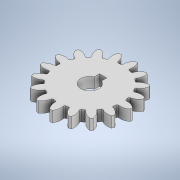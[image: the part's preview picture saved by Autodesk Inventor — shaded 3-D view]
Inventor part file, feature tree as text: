
AUTODESK INVENTOR PART (.ipt)
format: ipt  version: 2020 (Build 240168000, 168)  size: 262,656 bytes
history: native  units: mm
features: extrude x2, sketch x2, pattern_circular x1
ambient origin geometry x8: Origin, YZ Plane, XZ Plane, XY Plane, X Axis, Y Axis, Z Axis, Center Point
bodies: Solid1 (feature_tree)
feature tree (5):
  extrude  "Extrusion1"  Depth=3.0mm
  pattern_circular  "Circular Pattern2"  [2 undecoded]
  extrude  "Extrusion2"  TaperAngle=0.0deg  [1 undecoded]
  sketch  "Sketch1"  dims[d4=3.0mm d5=0.0mm d13=5.0mm]
  sketch  "Sketch2"  dims[d14=2.0mm d15=3.7mm d16=0.0mm d17=0.0mm d18=170.0mm d19=360.0deg d23=21.0mm d25=1.544118mm d26=1.235294mm d27=3.490659mm d28=19.733545mm d29=3.490659mm d30=0.308824mm d31=0.617647mm d32=0.9702mm]
note: 3 required parameter values undecoded (feature->parameter linkage not recoverable at this tier; creation-order binding heuristic only, values carry confidence <= 0.55)
